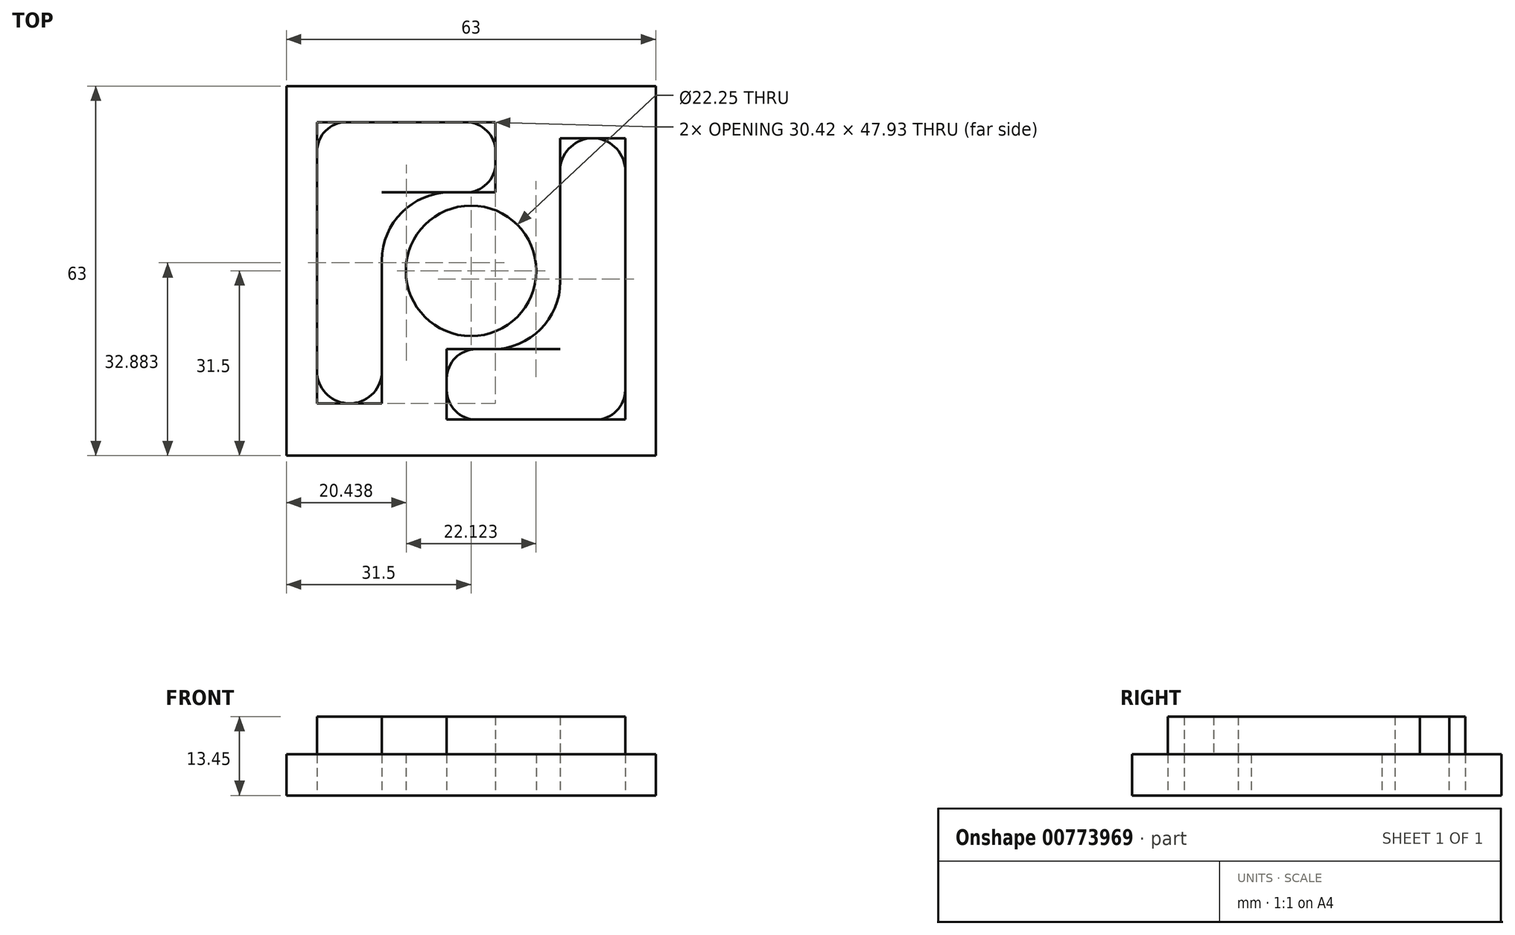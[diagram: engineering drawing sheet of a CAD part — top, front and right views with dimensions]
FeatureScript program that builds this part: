
annotation { "Feature Type Name" : "Feature", "Feature Type Description" : "" }
export const myFeature = defineFeature(function(context is Context, id is Id, definition is map)
    precondition{}
    {
        {
            var Q0;
            Q0=qCreatedBy(makeId("Top.planeOp"),FACE);
            var sketch = newSketch(context, id + "F0", { "sketchPlane" : qUnion([Q0])});
            skCircle(sketch, "E0", {"center": v(0, 0) * mm, "radius": 11.12 * mm});
            skLineSegment(sketch, "E1.bottom", {"start": v(-31.5, 31.5) * mm, "end": v(31.5, 31.5) * mm});
            skLineSegment(sketch, "E1.top", {"start": v(-31.5, -31.5) * mm, "end": v(31.5, -31.5) * mm});
            skLineSegment(sketch, "E1.left", {"start": v(-31.5, 31.5) * mm, "end": v(-31.5, -31.5) * mm});
            skLineSegment(sketch, "E1.right", {"start": v(31.5, 31.5) * mm, "end": v(31.5, -31.5) * mm});
            skLineSegment(sketch, "E2.bottom", {"start": v(-26.27, 13.37) * mm, "end": v(-15.2, 13.37) * mm});
            skLineSegment(sketch, "E2.top", {"start": v(-26.27, -22.58) * mm, "end": v(-15.2, -22.58) * mm});
            skLineSegment(sketch, "E2.left", {"start": v(-26.27, 13.37) * mm, "end": v(-26.27, -22.58) * mm});
            skLineSegment(sketch, "E2.right", {"start": v(-15.2, 13.37) * mm, "end": v(-15.2, -22.58) * mm});
            skLineSegment(sketch, "E3.bottom", {"start": v(-26.27, 13.37) * mm, "end": v(4.15, 13.37) * mm});
            skLineSegment(sketch, "E3.top", {"start": v(-26.27, 25.35) * mm, "end": v(4.15, 25.35) * mm});
            skLineSegment(sketch, "E3.left", {"start": v(-26.27, 13.37) * mm, "end": v(-26.27, 25.35) * mm});
            skLineSegment(sketch, "E3.right", {"start": v(4.15, 13.37) * mm, "end": v(4.15, 25.35) * mm});
            skLineSegment(sketch, "E4.1.0", {"start": v(26.27, -25.35) * mm, "end": v(-4.15, -25.35) * mm});
            skLineSegment(sketch, "E4.1.1", {"start": v(26.27, -13.37) * mm, "end": v(-4.15, -13.37) * mm});
            skLineSegment(sketch, "E4.1.2", {"start": v(15.2, -13.37) * mm, "end": v(15.2, 22.58) * mm});
            skLineSegment(sketch, "E4.1.3", {"start": v(-4.15, -13.37) * mm, "end": v(-4.15, -25.35) * mm});
            skLineSegment(sketch, "E4.1.4", {"start": v(26.27, -13.37) * mm, "end": v(26.27, -25.35) * mm});
            skLineSegment(sketch, "E4.1.5", {"start": v(26.27, -13.37) * mm, "end": v(26.27, 22.58) * mm});
            skLineSegment(sketch, "E4.1.6", {"start": v(26.27, 22.58) * mm, "end": v(15.2, 22.58) * mm});
            skSolve(sketch);
        }
        {
            var Q0;
            Q0=qSketchRegion(id+"F0",true);
            extrude(context, id + "F1", {"entities" : qUnion([Q0]), "depth" : 7 * mm, "offsetDistance" : 25 * mm});
        }
        {
            var Q0;
            Q0=makeQuery(id+"F1.opExtrude","CAP_FACE",FACE,{"disambiguationData":[OSD([sQuery(id+"F0.wireOp",EDGE,"E0"),sQuery(id+"F0.wireOp",EDGE,"E1.bottom"),sQuery(id+"F0.wireOp",EDGE,"E1.top"),sQuery(id+"F0.wireOp",EDGE,"E1.left"),sQuery(id+"F0.wireOp",EDGE,"E1.right"),sQuery(id+"F0.wireOp",EDGE,"E2.top"),sQuery(id+"F0.wireOp",EDGE,"E2.left"),sQuery(id+"F0.wireOp",EDGE,"E2.right"),sQuery(id+"F0.wireOp",EDGE,"E3.bottom"),sQuery(id+"F0.wireOp",EDGE,"E3.top"),sQuery(id+"F0.wireOp",EDGE,"E3.left"),sQuery(id+"F0.wireOp",EDGE,"E3.right"),sQuery(id+"F0.wireOp",EDGE,"E4.1.0"),sQuery(id+"F0.wireOp",EDGE,"E4.1.1"),sQuery(id+"F0.wireOp",EDGE,"E4.1.2"),sQuery(id+"F0.wireOp",EDGE,"E4.1.3"),sQuery(id+"F0.wireOp",EDGE,"E4.1.4"),sQuery(id+"F0.wireOp",EDGE,"E4.1.5"),sQuery(id+"F0.wireOp",EDGE,"E4.1.6")])],"isStart":false});
            var sketch = newSketch(context, id + "F2", { "sketchPlane" : qUnion([Q0])});
            skLineSegment(sketch, "E5", {"start": v(-26.27, 20.35) * mm, "end": v(-26.27, -17.58) * mm});
            skArc(sketch, "E6", {"start": v(-26.27, -17.58) * mm, "mid": v(-20.74, -22.6) * mm, "end": v(-15.2, -17.58) * mm});
            skLineSegment(sketch, "E7", {"start": v(-15.2, -17.58) * mm, "end": v(-15.2, 1.78) * mm});
            skArc(sketch, "E8", {"start": v(-3.62, 13.37) * mm, "mid": v(-11.82, 9.97) * mm, "end": v(-15.2, 1.78) * mm});
            skLineSegment(sketch, "E9", {"start": v(-3.62, 13.37) * mm, "end": v(-0.85, 13.37) * mm});
            skArc(sketch, "E10", {"start": v(-0.85, 13.37) * mm, "mid": v(2.68, 14.83) * mm, "end": v(4.15, 18.37) * mm});
            skLineSegment(sketch, "E11", {"start": v(4.15, 18.37) * mm, "end": v(4.15, 20.35) * mm});
            skArc(sketch, "E12", {"start": v(4.15, 20.35) * mm, "mid": v(2.68, 23.89) * mm, "end": v(-0.85, 25.35) * mm});
            skLineSegment(sketch, "E13", {"start": v(-0.85, 25.35) * mm, "end": v(-21.27, 25.35) * mm});
            skArc(sketch, "E14", {"start": v(-21.27, 25.35) * mm, "mid": v(-24.8, 23.89) * mm, "end": v(-26.27, 20.35) * mm});
            skArc(sketch, "E15.1.0", {"start": v(0.85, -13.37) * mm, "mid": v(-2.68, -14.83) * mm, "end": v(-4.15, -18.37) * mm});
            skArc(sketch, "E15.1.1", {"start": v(-4.15, -20.35) * mm, "mid": v(-2.68, -23.89) * mm, "end": v(0.85, -25.35) * mm});
            skLineSegment(sketch, "E15.1.2", {"start": v(0.85, -25.35) * mm, "end": v(21.27, -25.35) * mm});
            skArc(sketch, "E15.1.3", {"start": v(21.27, -25.35) * mm, "mid": v(24.8, -23.89) * mm, "end": v(26.27, -20.35) * mm});
            skArc(sketch, "E15.1.4", {"start": v(3.62, -13.37) * mm, "mid": v(11.82, -9.97) * mm, "end": v(15.2, -1.78) * mm});
            skLineSegment(sketch, "E15.1.5", {"start": v(15.2, 17.58) * mm, "end": v(15.2, -1.78) * mm});
            skArc(sketch, "E15.1.6", {"start": v(26.27, 17.58) * mm, "mid": v(20.74, 22.6) * mm, "end": v(15.2, 17.58) * mm});
            skLineSegment(sketch, "E15.1.7", {"start": v(26.27, -20.35) * mm, "end": v(26.27, 17.58) * mm});
            skLineSegment(sketch, "E15.1.8", {"start": v(-4.15, -18.37) * mm, "end": v(-4.15, -20.35) * mm});
            skLineSegment(sketch, "E15.1.9", {"start": v(3.62, -13.37) * mm, "end": v(0.85, -13.37) * mm});
            skPoint(sketch, "E15.center", {"position": v(0, 0) * mm});
            skSolve(sketch);
        }
        {
            var Q0;
            Q0 = qSketchRegion(id + "F2", true);
            extrude(context, id + "F3", {"entities" : qUnion([Q0]), "depth" : 6.45 * mm, "offsetDistance" : 25 * mm});
        }
    });
